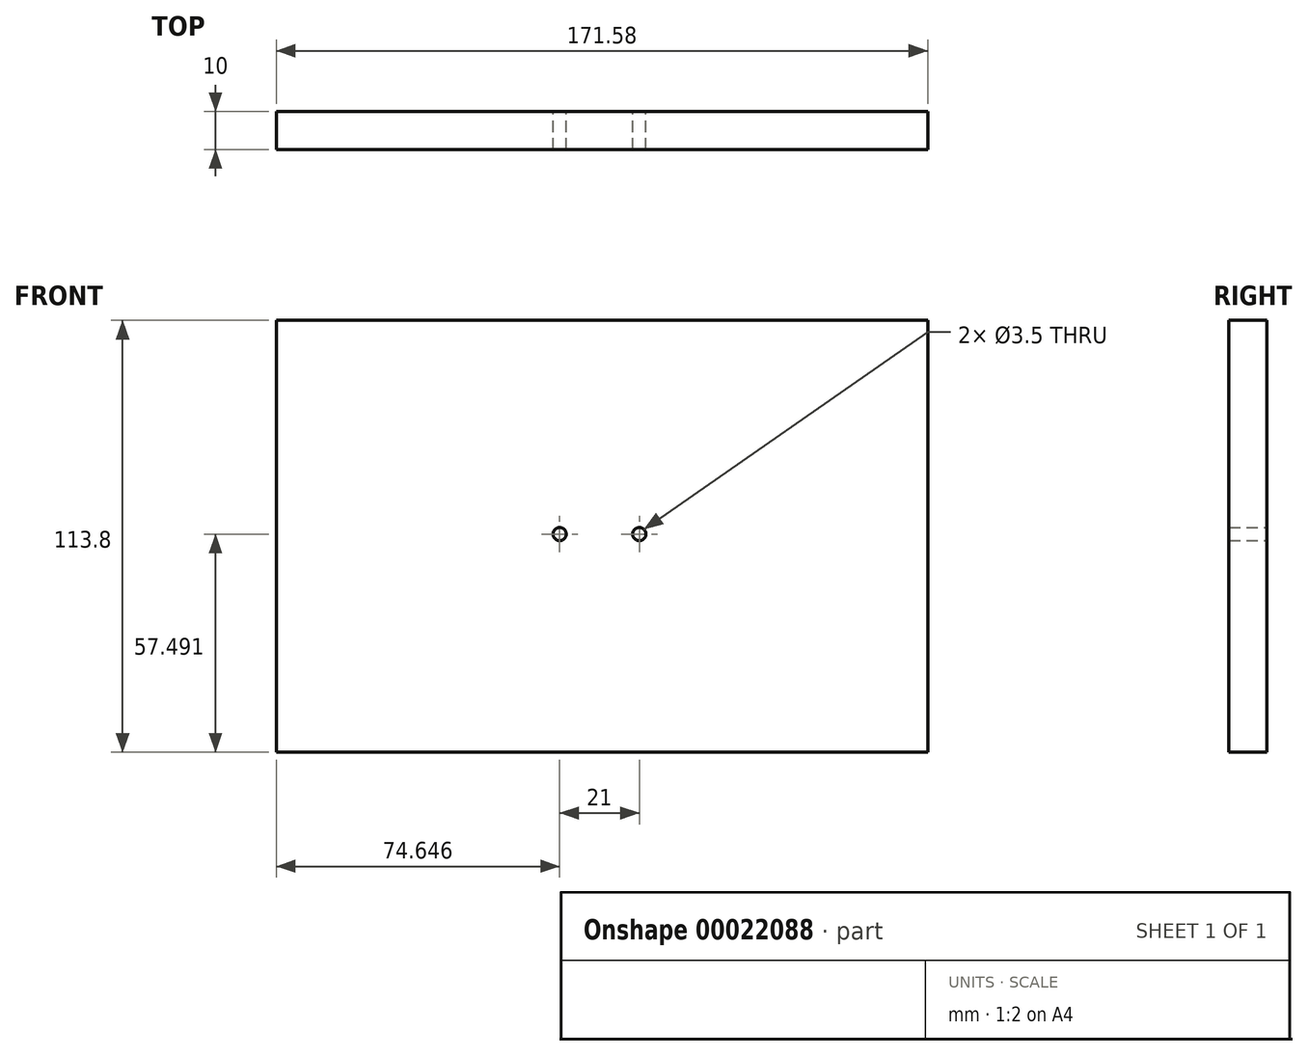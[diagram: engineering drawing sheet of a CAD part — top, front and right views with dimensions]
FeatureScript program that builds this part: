
annotation { "Feature Type Name" : "Feature", "Feature Type Description" : "" }
export const myFeature = defineFeature(function(context is Context, id is Id, definition is map)
    precondition{}
    {
        {
            var Q0;
            Q0=qCreatedBy(makeId("Front.planeOp"),FACE);
            var sketch = newSketch(context, id + "F0", { "sketchPlane" : qUnion([Q0])});
            skCircle(sketch, "E0", {"center": v(-21.7, -6.6) * mm, "radius": 1.75 * mm});
            skCircle(sketch, "E1", {"center": v(-0.7, -6.6) * mm, "radius": 1.75 * mm});
            skLineSegment(sketch, "E2.bottom", {"start": v(-96.35, 49.71) * mm, "end": v(75.23, 49.71) * mm});
            skLineSegment(sketch, "E2.top", {"start": v(-96.35, -64.09) * mm, "end": v(75.23, -64.09) * mm});
            skLineSegment(sketch, "E2.left", {"start": v(-96.35, 49.71) * mm, "end": v(-96.35, -64.09) * mm});
            skLineSegment(sketch, "E2.right", {"start": v(75.23, 49.71) * mm, "end": v(75.23, -64.09) * mm});
            skSolve(sketch);
        }
        {
            var Q0;
            Q0=makeQuery(id+"F0.imprint","IMPRINT",FACE,{"disambiguationData":[TD([[makeQuery(id+"F0.imprint","IMPRINT",EDGE,{"derivedFrom":sQuery(id+"F0.wireOp",EDGE,"E0")}),-1.0]])]});
            extrude(context, id + "F1", {"entities" : qUnion([Q0]), "depth" : 10 * mm});
        }
    });
